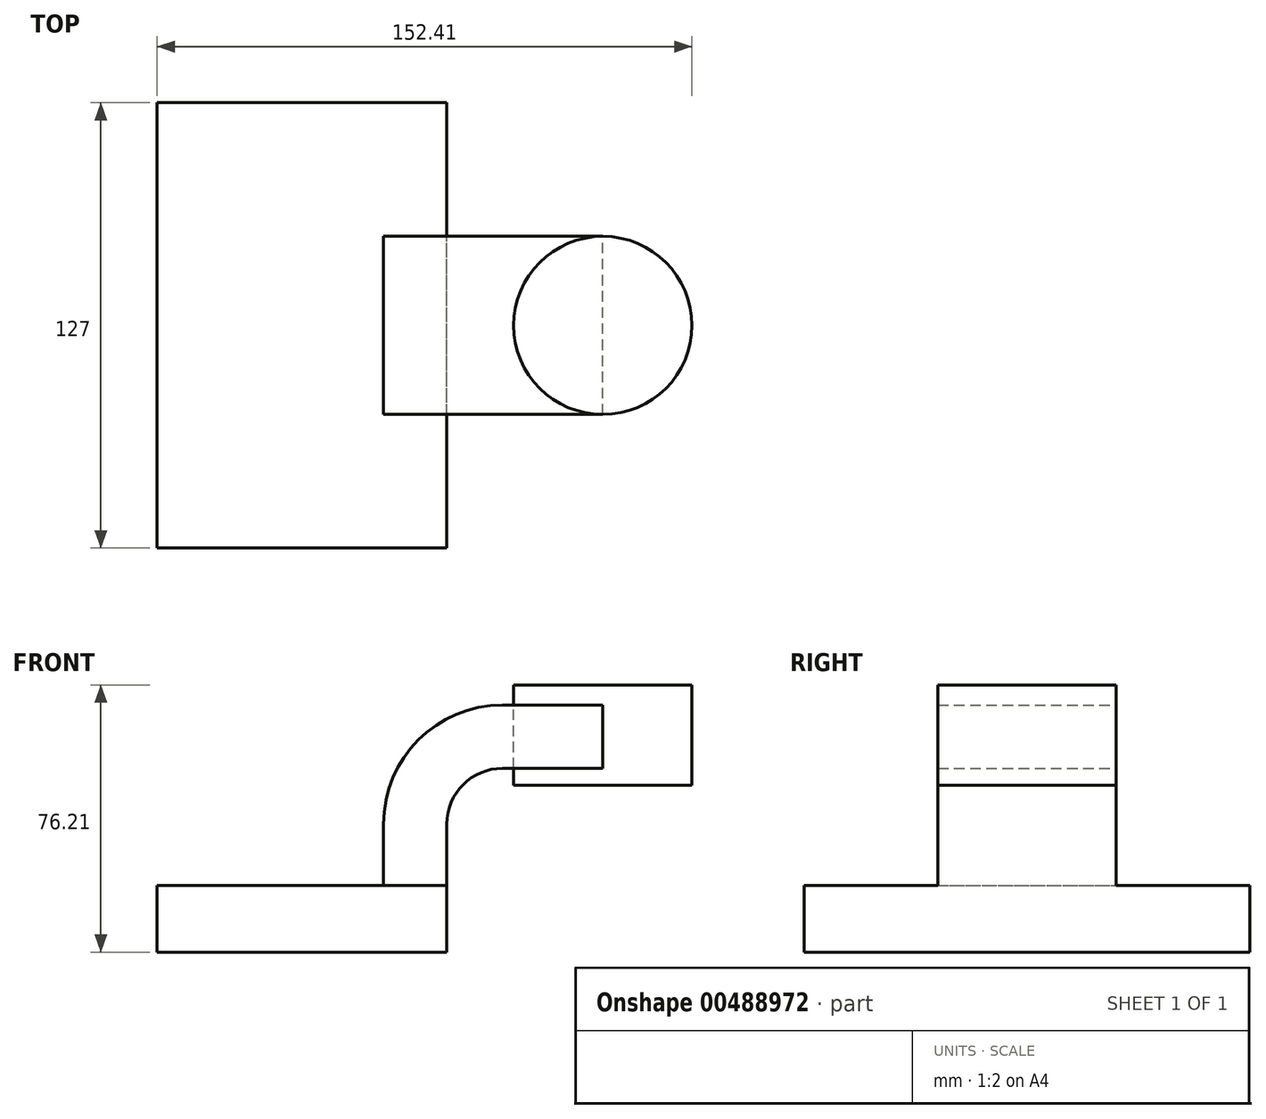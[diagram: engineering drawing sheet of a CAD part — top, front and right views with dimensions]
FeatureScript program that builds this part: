
annotation { "Feature Type Name" : "Feature", "Feature Type Description" : "" }
export const myFeature = defineFeature(function(context is Context, id is Id, definition is map)
    precondition{}
    {
        {
            var Q0;
            Q0=qCreatedBy(makeId("Front.planeOp"),FACE);
            var sketch = newSketch(context, id + "F0", { "sketchPlane" : qUnion([Q0])});
            skLineSegment(sketch, "E0.bottom", {"start": v(41.28, -9.52) * mm, "end": v(-41.28, -9.53) * mm});
            skLineSegment(sketch, "E0.top", {"start": v(41.28, 9.53) * mm, "end": v(-41.28, 9.53) * mm});
            skLineSegment(sketch, "E0.left", {"start": v(41.28, -9.52) * mm, "end": v(41.28, 9.53) * mm});
            skLineSegment(sketch, "E0.right", {"start": v(-41.28, -9.53) * mm, "end": v(-41.28, 9.53) * mm});
            skPoint(sketch, "E0.middle", {"position": v(0, 0) * mm});
            skLineSegment(sketch, "E1.top", {"start": v(111.12, 66.68) * mm, "end": v(60.33, 66.68) * mm});
            skLineSegment(sketch, "E1.left", {"start": v(111.12, 38.1) * mm, "end": v(111.12, 66.68) * mm});
            skPoint(sketch, "E1.middle", {"position": v(85.72, 52.39) * mm});
            skLineSegment(sketch, "E2", {"start": v(41.28, 9.53) * mm, "end": v(41.28, 27) * mm});
            skArc(sketch, "E3", {"start": v(41.27, 27) * mm, "mid": v(45.92, 38.23) * mm, "end": v(57.15, 42.88) * mm});
            skLineSegment(sketch, "E4", {"start": v(57.15, 42.88) * mm, "end": v(85.72, 42.88) * mm});
            skLineSegment(sketch, "E5.0", {"start": v(57.15, 60.91) * mm, "end": v(85.72, 60.91) * mm});
            skArc(sketch, "E5.1", {"start": v(23.24, 27) * mm, "mid": v(33.17, 50.98) * mm, "end": v(57.15, 60.91) * mm});
            skLineSegment(sketch, "E5.2", {"start": v(23.24, 9.53) * mm, "end": v(23.24, 27) * mm});
            skFitSpline(sketch, "E6", {"points": [v(-41.28, 9.52) * mm, v(60.33, 66.68) * mm], "startDerivative": vector(46.3, 115.69) * mm, "endDerivative": vector(109.01, 3.43) * mm});
            skLineSegment(sketch, "E7", {"start": v(85.72, 66.68) * mm, "end": v(85.72, 38.1) * mm});
            skLineSegment(sketch, "E8", {"start": v(60.33, 66.68) * mm, "end": v(60.33, 60.91) * mm});
            skPoint(sketch, "E8.endSnap0", {"position": v(71.44, 60.91) * mm});
            skLineSegment(sketch, "E9", {"start": v(60.33, 42.88) * mm, "end": v(60.33, 38.1) * mm});
            skLineSegment(sketch, "E10", {"start": v(60.33, 38.1) * mm, "end": v(111.12, 38.1) * mm});
            skSolve(sketch);
        }
        {
            var Q0;
            Q0=makeQuery(id+"F0.imprint","IMPRINT",FACE,{"disambiguationData":[TD([[makeQuery(id+"F0.imprint","IMPRINT",EDGE,{"derivedFrom":sQuery(id+"F0.wireOp",EDGE,"E0.bottom")}),-1.0]])]});
            extrude(context, id + "F1", {"entities" : qUnion([Q0]), "endBound" : BoundingType.SYMMETRIC, "depth" : 127 * mm});
        }
        {
            var Q0;
            {var subQ1=sQuery(id+"F0.wireOp",EDGE,"E1.bottom");Q0=makeQuery(id+"F0.imprint","IMPRINT",FACE,{"disambiguationData":[TD([[makeQuery(id+"F0.imprint","IMPRINT",EDGE,{"derivedFrom":subQ1}),-1.0]])]});}
            var sketch = newSketch(context, id + "F2", { "sketchPlane" : qUnion([Q0])});
            skLineSegment(sketch, "E11", {"start": v(86.09, 59.98) * mm, "end": v(86.09, 42.77) * mm});
            skSolve(sketch);
        }
        {
            var Q0;
            {var subQ1=sQuery(id+"F0.wireOp",EDGE,"E2");Q0=makeQuery(id+"F0.imprint","IMPRINT",FACE,{"disambiguationData":[TD([[makeQuery(id+"F0.imprint","IMPRINT",EDGE,{"derivedFrom":subQ1}),1.0]])]});}
            var Q1;
            {var subQ1=sQuery(id+"F0.wireOp",EDGE,"E1.bottom");Q1=makeQuery(id+"F2.imprint","IMPRINT",FACE,{"disambiguationData":[TD([[makeQuery(id+"F2.imprint","IMPRINT",EDGE,{"derivedFrom":makeQuery(id+"F0.imprint","IMPRINT",EDGE,{"derivedFrom":subQ1})}),-1.0]])]});}
            extrude(context, id + "F3", {"entities" : qUnion([Q0, Q1]), "operationType" : NewBodyOperationType.ADD, "endBound" : BoundingType.SYMMETRIC, "depth" : 50.8 * mm});
        }
        {
            var Q0;
            {var subQ0=sQuery(id+"F0.wireOp",EDGE,"E5.1");Q0=makeQuery(id+"F0.imprint","IMPRINT",FACE,{"disambiguationData":[TD([[makeQuery(id+"F0.imprint","IMPRINT",EDGE,{"derivedFrom":subQ0}),1.0]])]});}
            extrude(context, id + "F4", {"entities" : qUnion([Q0]), "operationType" : NewBodyOperationType.ADD, "endBound" : BoundingType.SYMMETRIC, "depth" : 15.88 * mm});
        }
        {
            var Q0;
            {var subQ3=sQuery(id+"F0.wireOp",EDGE,"E1.left");Q0=makeQuery(id+"F0.imprint","IMPRINT",FACE,{"disambiguationData":[TD([[makeQuery(id+"F0.imprint","IMPRINT",EDGE,{"derivedFrom":subQ3}),1.0]])]});}
            var Q1;
            Q1=sQuery(id+"F0.wireOp",EDGE,"E7");
            revolve(context, id + "F5", {"entities" : qUnion([Q0]), "axis" : qUnion([Q1]), "revolveType" : RevolveType.FULL});
        }
    });
